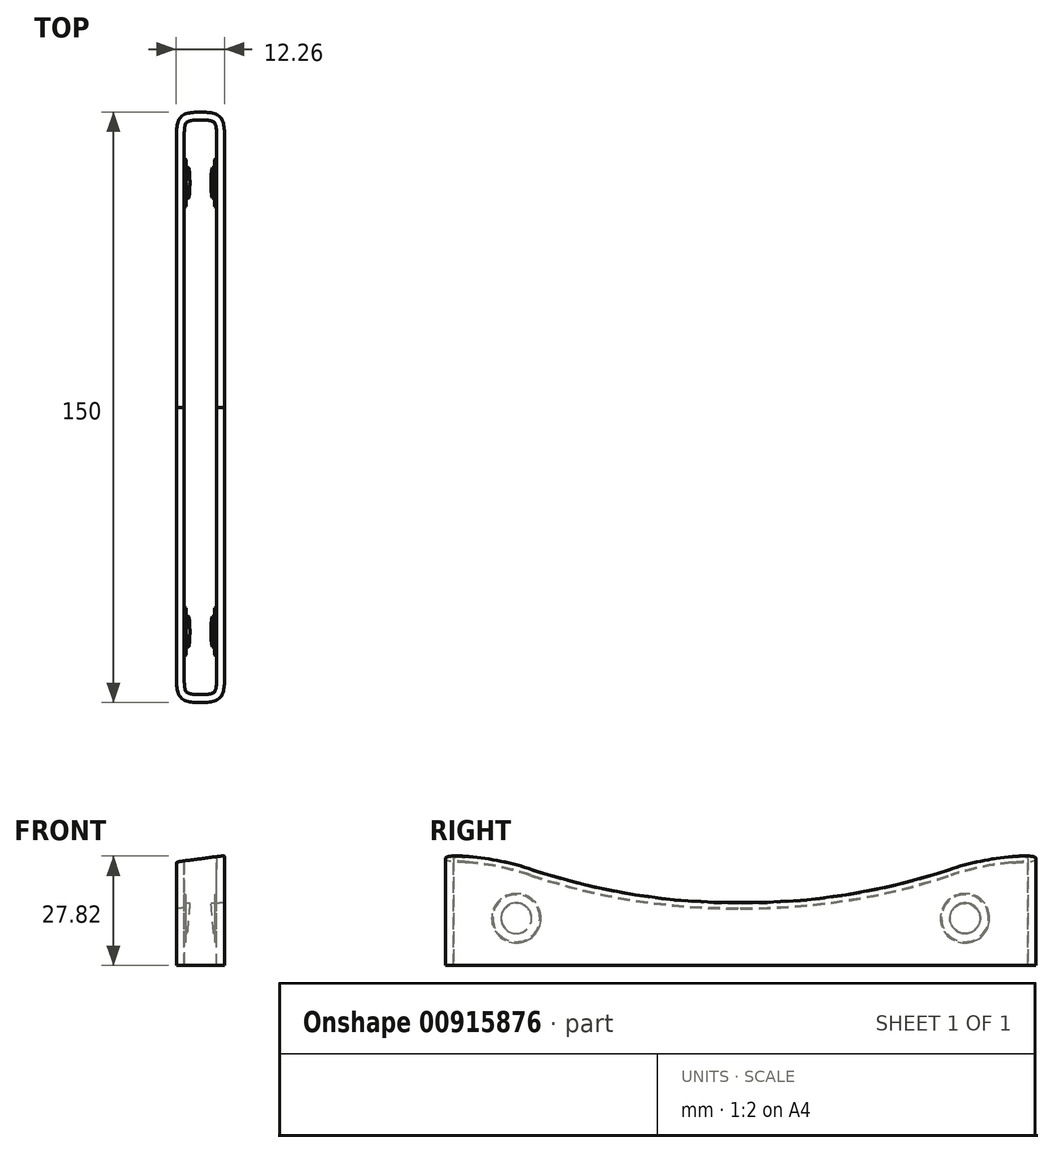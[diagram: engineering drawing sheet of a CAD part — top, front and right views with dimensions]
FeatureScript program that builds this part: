
annotation { "Feature Type Name" : "Feature", "Feature Type Description" : "" }
export const myFeature = defineFeature(function(context is Context, id is Id, definition is map)
    precondition{}
    {
        {
            var Q0;
            Q0=qCreatedBy(makeId("Top.planeOp"),FACE);
            var sketch = newSketch(context, id + "F0", { "sketchPlane" : qUnion([Q0])});
            skLineSegment(sketch, "E0.bottom", {"start": v(-6.12, 75) * mm, "end": v(6.13, 75) * mm});
            skLineSegment(sketch, "E0.top", {"start": v(-6.13, -75) * mm, "end": v(6.12, -75) * mm});
            skLineSegment(sketch, "E0.left", {"start": v(-6.12, 75) * mm, "end": v(-6.13, -75) * mm});
            skLineSegment(sketch, "E0.right", {"start": v(6.13, 75) * mm, "end": v(6.12, -75) * mm});
            skPoint(sketch, "E0.middle", {"position": v(0, 0) * mm});
            skSolve(sketch);
        }
        {
            var Q0;
            Q0=qSketchRegion(id+"F0",true);
            extrude(context, id + "F1", {"entities" : qUnion([Q0]), "depth" : 35 * mm, "offsetDistance" : 25 * mm});
        }
        {
            var Q0;
            Q0=makeQuery(id+"F1.opExtrude","SWEPT_EDGE",EDGE,{"disambiguationData":[OSD([sQuery(id+"F0.wireOp",EDGE,"E0.top"),sQuery(id+"F0.wireOp",EDGE,"E0.right")])]});
            var Q1;
            Q1=makeQuery(id+"F1.opExtrude","SWEPT_EDGE",EDGE,{"disambiguationData":[OSD([sQuery(id+"F0.wireOp",EDGE,"E0.top"),sQuery(id+"F0.wireOp",EDGE,"E0.left")])]});
            var Q2;
            Q2=makeQuery(id+"F1.opExtrude","SWEPT_EDGE",EDGE,{"disambiguationData":[OSD([sQuery(id+"F0.wireOp",EDGE,"E0.bottom"),sQuery(id+"F0.wireOp",EDGE,"E0.right")])]});
            var Q3;
            Q3=makeQuery(id+"F1.opExtrude","SWEPT_EDGE",EDGE,{"disambiguationData":[OSD([sQuery(id+"F0.wireOp",EDGE,"E0.bottom"),sQuery(id+"F0.wireOp",EDGE,"E0.left")])]});
            fillet(context, id + "F2", {"entities" : qUnion([Q0, Q1, Q2, Q3]), "radius" : 6 * mm, "tangentPropagation" : true, "rho" : .6, "defaultsChanged" : true, "vertexSettings" : [], "crossSection" : FilletCrossSection.CONIC, "allowEdgeOverflow" : false});
        }
        {
            var Q0;
            Q0=makeQuery(id+"F14.boolean.opBoolean","COPY",FACE,{"derivedFrom":makeQuery(id+"F14.opExtrude","SWEPT_FACE",FACE,{"disambiguationData":[OSD([sQuery(id+"F13.wireOp",EDGE,"E11")])]})});
            var Q1;
            Q1=makeQuery(id+"F1.opExtrude","CAP_FACE",FACE,{"disambiguationData":[OSD([sQuery(id+"F0.wireOp",EDGE,"E0.bottom"),sQuery(id+"F0.wireOp",EDGE,"E0.top"),sQuery(id+"F0.wireOp",EDGE,"E0.left"),sQuery(id+"F0.wireOp",EDGE,"E0.right")])],"isStart":true});
            var Q2;
            Q2=makeQuery(id+"F1.opExtrude","CAP_FACE",FACE,{"disambiguationData":[OSD([sQuery(id+"F0.wireOp",EDGE,"E0.bottom"),sQuery(id+"F0.wireOp",EDGE,"E0.top"),sQuery(id+"F0.wireOp",EDGE,"E0.left"),sQuery(id+"F0.wireOp",EDGE,"E0.right")])],"isStart":false});
            shell(context, id + "F3", {"entities" : qUnion([Q0, Q1, Q2]), "thickness" : 2 * mm});
        }
        {
            var Q0;
            Q0=makeQuery(id+"F3.opShell","OFFSET_FACE",FACE,{"disambiguationData":[OSD([sQuery(id+"F0.wireOp",EDGE,"E0.bottom")])]});
            cPlane(context, id + "F4", {"entities" : qUnion([Q0]), "cplaneType" : CPlaneType.OFFSET, "offset" : 16 * mm, "width" : 150 * mm, "height" : 150 * mm});
        }
        {
            var Q0;
            Q0=makeQuery(id+"F3.opShell","OFFSET_FACE",FACE,{"disambiguationData":[OSD([sQuery(id+"F0.wireOp",EDGE,"E0.right")])]});
            var sketch = newSketch(context, id + "F5", { "sketchPlane" : qUnion([Q0])});
            skCircle(sketch, "E1", {"center": v(-57, 12) * mm, "radius": 6.25 * mm});
            skSolve(sketch);
        }
        {
            var Q0;
            Q0=qSketchRegion(id+"F5",true);
            var Q1;
            Q1=makeQuery(id+"FLqfYe4GLTb1ksn_1.opExtrude","SWEPT_FACE",FACE,{"disambiguationData":[OSD([sQuery(id+"FB4pY4kdx2plPhE_1.wireOp",EDGE,"4Bwas7ee-6Ia2-9Bo0-NcGV-Cqd8jdgVMGEA")])]});
            extrude(context, id + "F6", {"entities" : qUnion([Q0]), "operationType" : NewBodyOperationType.ADD, "depth" : .5 * mm, "endBoundEntityFace" : qUnion([Q1]), "offsetDistance" : 25 * mm, "hasDraft" : true, "draftAngle" : 30 * degree, "draftPullDirection" : true, "hasSecondDirectionDraft" : true, "secondDirectionDraftAngle" : 15 * degree, "secondDirectionDraftPullDirection" : true});
        }
        {
            var Q0;
            Q0=makeQuery(id+"F3.opShell","OFFSET_FACE",FACE,{"disambiguationData":[OSD([sQuery(id+"F0.wireOp",EDGE,"E0.left")])]});
            var sketch = newSketch(context, id + "F7", { "sketchPlane" : qUnion([Q0])});
            skCircle(sketch, "E2.0", {"center": v(57, 12) * mm, "radius": 6.25 * mm});
            skSolve(sketch);
        }
        {
            var Q0;
            Q0=qSketchRegion(id+"F7",true);
            extrude(context, id + "F8", {"entities" : qUnion([Q0]), "operationType" : NewBodyOperationType.ADD, "depth" : .5 * mm, "offsetDistance" : 25 * mm, "hasDraft" : true, "draftAngle" : 30 * degree, "draftPullDirection" : true});
        }
        {
            var Q0;
            Q0=makeQuery(id+"F6.opExtrude","CAP_FACE",FACE,{"disambiguationData":[OSD([sQuery(id+"F5.wireOp",EDGE,"E1")])],"isStart":false});
            var sketch = newSketch(context, id + "F9", { "sketchPlane" : qUnion([Q0])});
            skCircle(sketch, "E3", {"center": v(-57, 12) * mm, "radius": 3.9 * mm});
            skLineSegment(sketch, "E4", {"start": v(-57, 8.1) * mm, "end": v(-57, 15.9) * mm, "construction": true});
            skSolve(sketch);
        }
        {
            var Q0;
            Q0=qSketchRegion(id+"F9",true);
            var Q1;
            Q1=makeQuery(id+"F8.opExtrude","CAP_FACE",FACE,{"disambiguationData":[OSD([sQuery(id+"F7.wireOp",EDGE,"E2.0")])],"isStart":false});
            var Q2;
            Q2=makeQuery(id+"F0P6d4zUNtGuZU6_1.opExtrude","CAP_FACE",FACE,{"disambiguationData":[OSD([sQuery(id+"Fkxqu71xXAKCoJv_1.wireOp",EDGE,"4c5a5ca7-3958-4f76-a320-1f03bb76a817.0")])],"isStart":false});
            extrude(context, id + "F10", {"entities" : qUnion([Q0]), "operationType" : NewBodyOperationType.ADD, "endBound" : BoundingType.UP_TO_SURFACE, "depth" : 25 * mm, "endBoundEntityFace" : qUnion([Q1]), "offsetDistance" : 25 * mm});
        }
        {
            var Q0;
            Q0=qCreatedBy(id+"F4.planeOp",FACE);
            var sketch = newSketch(context, id + "F11", { "sketchPlane" : qUnion([Q0])});
            skLineSegment(sketch, "E5", {"start": v(-2.7, 15.9) * mm, "end": v(-3.37, 8.1) * mm});
            skLineSegment(sketch, "E6", {"start": v(-3.37, 8.1) * mm, "end": v(3.38, 8.1) * mm});
            skLineSegment(sketch, "E7", {"start": v(2.7, 15.9) * mm, "end": v(3.38, 8.1) * mm});
            skLineSegment(sketch, "E8", {"start": v(2.7, 15.9) * mm, "end": v(-2.7, 15.9) * mm});
            skLineSegment(sketch, "E9", {"start": v(3.38, 8.1) * mm, "end": v(3.63, 8.1) * mm, "construction": true});
            skLineSegment(sketch, "E10", {"start": v(-3.37, 8.1) * mm, "end": v(-3.62, 8.1) * mm, "construction": true});
            skSolve(sketch);
        }
        {
            var Q0;
            Q0=qSketchRegion(id+"F11",true);
            var Q1;
            Q1=makeQuery(id+"F3.opShell","OFFSET_FACE",FACE,{"disambiguationData":[OSD([sQuery(id+"F0.wireOp",EDGE,"E0.bottom"),sQuery(id+"F0.wireOp",EDGE,"E0.left")])]});
            extrude(context, id + "F12", {"entities" : qUnion([Q0]), "operationType" : NewBodyOperationType.REMOVE, "endBound" : BoundingType.SYMMETRIC, "oppositeDirection" : true, "depth" : 12 * mm, "endBoundEntityFace" : qUnion([Q1]), "offsetDistance" : 25 * mm});
        }
        {
            var Q0;
            Q0=makeQuery(id+"F1.opExtrude","SWEPT_FACE",FACE,{"disambiguationData":[OSD([sQuery(id+"F0.wireOp",EDGE,"E0.right")])]});
            var sketch = newSketch(context, id + "F13", { "sketchPlane" : qUnion([Q0])});
            skArc(sketch, "E11", {"start": v(0, 16) * mm, "mid": v(26.8, 17.98) * mm, "end": v(52.9, 24.34) * mm});
            skLineSegment(sketch, "E12", {"start": v(-75, 35) * mm, "end": v(75, 35) * mm});
            skCircle(sketch, "E13", {"center": v(57, 12) * mm, "radius": 11 * mm, "construction": true});
            skArc(sketch, "E14", {"start": v(0, 2.94) * mm, "mid": v(53.33, 23.3) * mm, "end": v(79.5, 74.05) * mm, "construction": true});
            skLineSegment(sketch, "E15", {"start": v(0, 2.94) * mm, "end": v(-29.27, 2.94) * mm, "construction": true});
            skLineSegment(sketch, "E16", {"start": v(-24.7, 7.25) * mm, "end": v(0, 7.25) * mm, "construction": true});
            skPoint(sketch, "E16.endSnap0", {"position": v(0, 16) * mm});
            skArc(sketch, "E17", {"start": v(0, 7.25) * mm, "mid": v(58.45, 26.1) * mm, "end": v(94.85, 75.57) * mm, "construction": true});
            skArc(sketch, "E18", {"start": v(75, 27.92) * mm, "mid": v(63.8, 27.01) * mm, "end": v(52.9, 24.34) * mm});
            skLineSegment(sketch, "E19", {"start": v(75, 27.92) * mm, "end": v(78.45, 27.92) * mm, "construction": true});
            skLineSegment(sketch, "E20", {"start": v(75, 27.92) * mm, "end": v(75, 35) * mm});
            skCircle(sketch, "E21", {"center": v(57, 12) * mm, "radius": 13 * mm, "construction": true});
            skLineSegment(sketch, "E22", {"start": v(0, 16) * mm, "end": v(-19.88, 16.17) * mm, "construction": true});
            skLineSegment(sketch, "E23", {"start": v(0, 16) * mm, "end": v(0, 35) * mm});
            skSolve(sketch);
        }
        {
            var Q0;
            Q0=qSketchRegion(id+"F13",true);
            extrude(context, id + "F14", {"entities" : qUnion([Q0]), "operationType" : NewBodyOperationType.REMOVE, "endBound" : BoundingType.THROUGH_ALL, "oppositeDirection" : true, "depth" : 25 * mm, "offsetDistance" : 25 * mm, "hasDraft" : true, "draftAngle" : 7.5 * degree});
        }
        {
            var Q0;
            Q0=qCreatedBy(makeId("Front.planeOp"),FACE);
            var sketch = newSketch(context, id + "F15", { "sketchPlane" : qUnion([Q0])});
            skLineSegment(sketch, "E24.bottom", {"start": v(6.13, 0) * mm, "end": v(-6.13, 0) * mm});
            skLineSegment(sketch, "E24.top", {"start": v(6.12, 63.43) * mm, "end": v(-6.13, 63.43) * mm});
            skLineSegment(sketch, "E24.left", {"start": v(6.13, 0) * mm, "end": v(6.12, 63.43) * mm});
            skLineSegment(sketch, "E24.right", {"start": v(-6.13, 0) * mm, "end": v(-6.13, 63.43) * mm});
            skSolve(sketch);
        }
        {
            var Q0;
            Q0 = qSketchRegion(id + "F15", true);
            extrude(context, id + "F16", {"entities" : qUnion([Q0]), "operationType" : NewBodyOperationType.REMOVE, "endBound" : BoundingType.THROUGH_ALL, "depth" : 25 * mm, "offsetDistance" : 25 * mm});
        }
        {
            var Q0;
            Q0=makeQuery(id+"F1.opExtrude","SWEPT_BODY",BODY,{"disambiguationData":[OSD([sQuery(id+"F0.wireOp",EDGE,"E0.bottom"),sQuery(id+"F0.wireOp",EDGE,"E0.top"),sQuery(id+"F0.wireOp",EDGE,"E0.left"),sQuery(id+"F0.wireOp",EDGE,"E0.right")])]});
            var Q1;
            Q1=qCreatedBy(makeId("Front.planeOp"),FACE);
            mirror(context, id + "F17", {"operationType" : NewBodyOperationType.ADD, "entities" : qUnion([Q0]), "mirrorPlane" : qUnion([Q1])});
        }
    });
